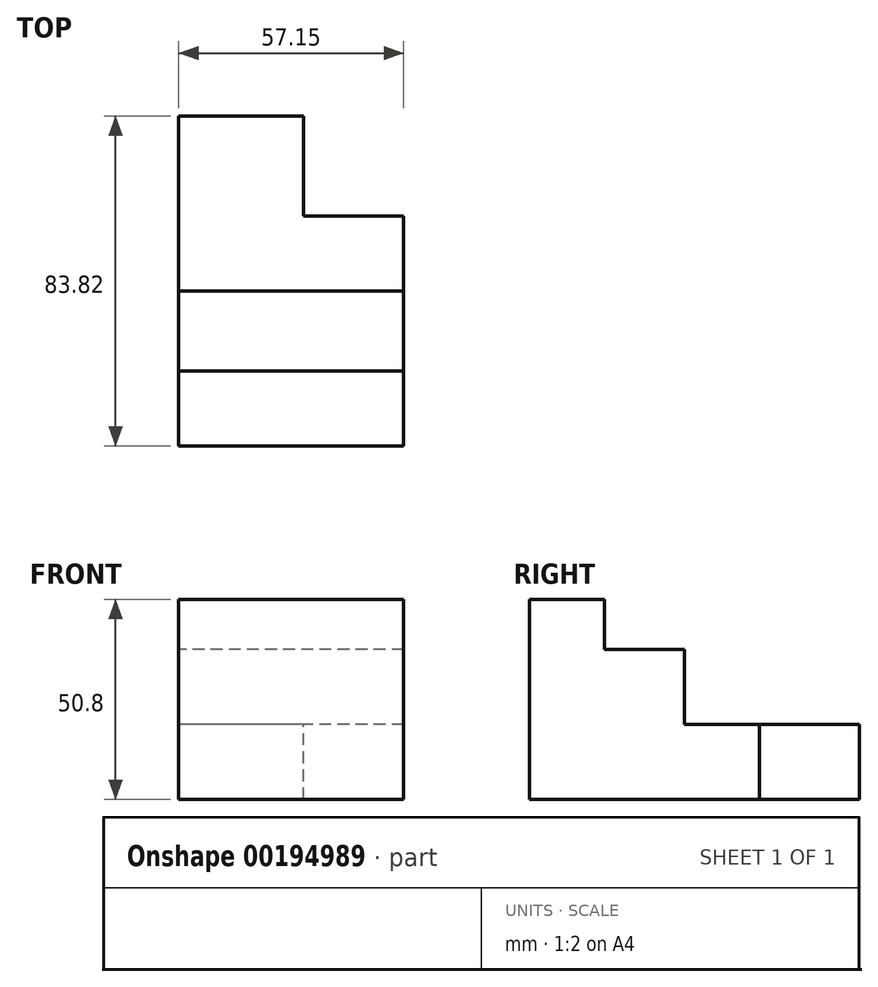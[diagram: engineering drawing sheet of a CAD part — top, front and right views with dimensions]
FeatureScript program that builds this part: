
annotation { "Feature Type Name" : "Feature", "Feature Type Description" : "" }
export const myFeature = defineFeature(function(context is Context, id is Id, definition is map)
    precondition{}
    {
        {
            var Q0;
            Q0=qCreatedBy(makeId("Right.planeOp"),FACE);
            var sketch = newSketch(context, id + "F0", { "sketchPlane" : qUnion([Q0])});
            skLineSegment(sketch, "E0", {"start": v(0, 0) * mm, "end": v(83.82, 0) * mm});
            skLineSegment(sketch, "E1", {"start": v(83.82, 0) * mm, "end": v(83.82, 19.05) * mm});
            skLineSegment(sketch, "E2", {"start": v(83.82, 19.05) * mm, "end": v(39.37, 19.05) * mm});
            skLineSegment(sketch, "E3", {"start": v(39.37, 19.05) * mm, "end": v(39.37, 38.1) * mm});
            skLineSegment(sketch, "E4", {"start": v(39.37, 38.1) * mm, "end": v(19.05, 38.1) * mm});
            skLineSegment(sketch, "E5", {"start": v(19.05, 38.1) * mm, "end": v(19.05, 50.8) * mm});
            skLineSegment(sketch, "E6", {"start": v(19.05, 50.8) * mm, "end": v(0, 50.8) * mm});
            skLineSegment(sketch, "E7", {"start": v(0, 50.8) * mm, "end": v(0, 0) * mm});
            skSolve(sketch);
        }
        {
            var Q0;
            Q0 = qSketchRegion(id + "F0", true);
            extrude(context, id + "F1", {"entities" : qUnion([Q0]), "depth" : 57.15 * mm});
        }
        {
            var Q0;
            Q0=makeQuery(id+"F1.opExtrude","SWEPT_FACE",FACE,{"disambiguationData":[OSD([sQuery(id+"F0.wireOp",EDGE,"E2")])]});
            var sketch = newSketch(context, id + "F2", { "sketchPlane" : qUnion([Q0])});
            skLineSegment(sketch, "E8.bottom", {"start": v(57.15, 83.82) * mm, "end": v(31.75, 83.82) * mm});
            skLineSegment(sketch, "E8.top", {"start": v(57.15, 58.42) * mm, "end": v(31.75, 58.42) * mm});
            skLineSegment(sketch, "E8.left", {"start": v(57.15, 83.82) * mm, "end": v(57.15, 58.42) * mm});
            skLineSegment(sketch, "E8.right", {"start": v(31.75, 83.82) * mm, "end": v(31.75, 58.42) * mm});
            skSolve(sketch);
        }
        {
            var Q0;
            Q0 = qSketchRegion(id + "F2", true);
            extrude(context, id + "F3", {"entities" : qUnion([Q0]), "operationType" : NewBodyOperationType.REMOVE, "endBound" : BoundingType.THROUGH_ALL, "oppositeDirection" : true, "depth" : 25.4 * mm});
        }
    });
